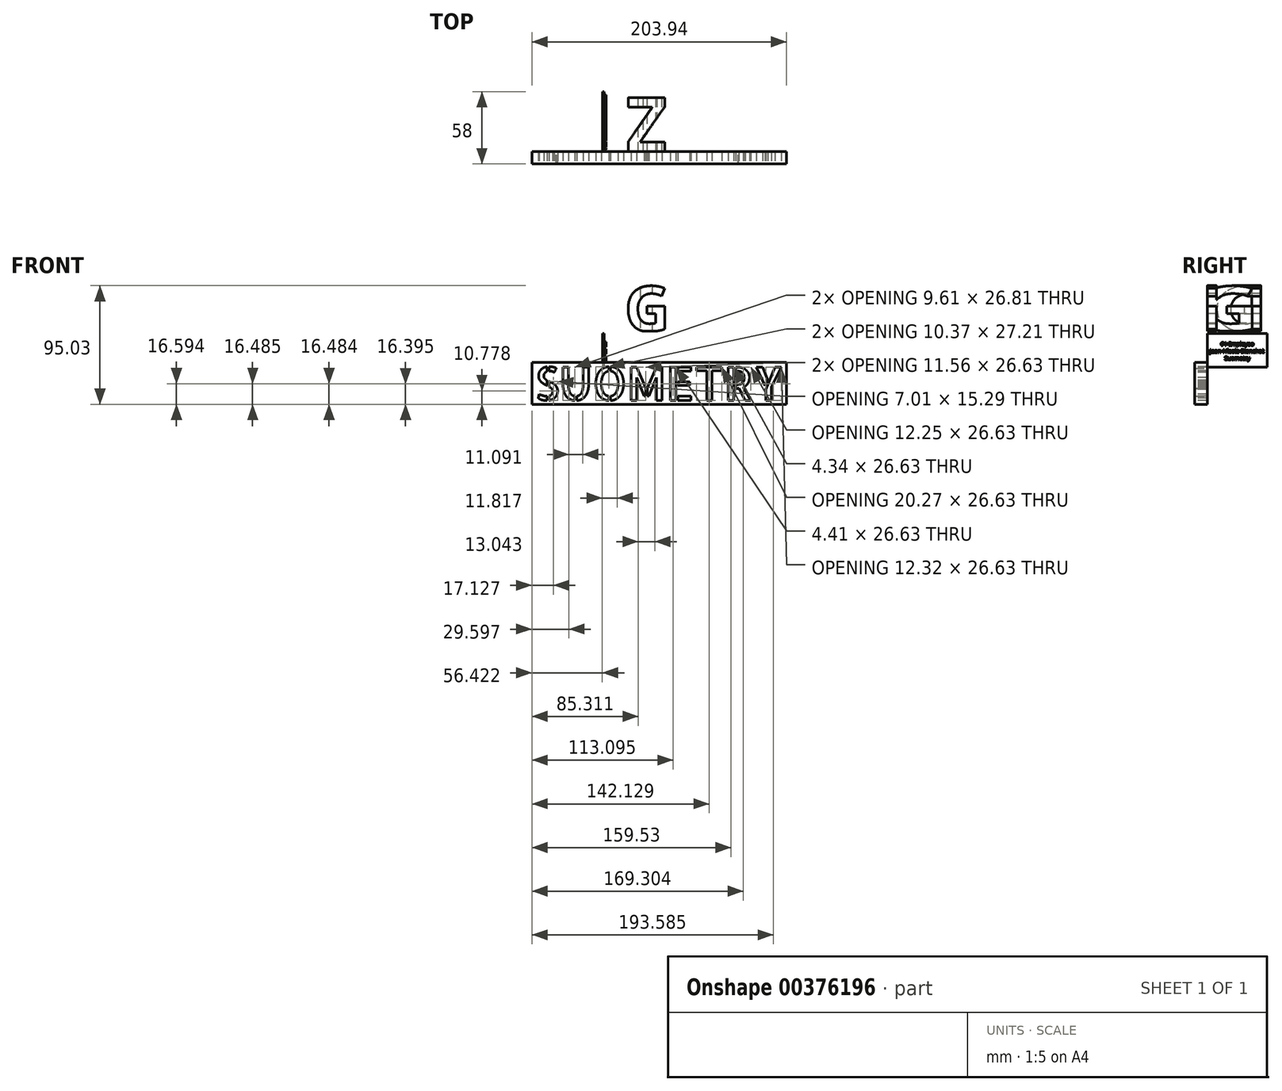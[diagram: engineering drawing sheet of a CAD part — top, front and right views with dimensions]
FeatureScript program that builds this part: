
annotation { "Feature Type Name" : "Feature", "Feature Type Description" : "" }
export const myFeature = defineFeature(function(context is Context, id is Id, definition is map)
    precondition{}
    {
        {
            var Q0;
            Q0=qCreatedBy(makeId("Front.planeOp"),FACE);
            var sketch = newSketch(context, id + "F0", { "sketchPlane" : qUnion([Q0])});
            skText(sketch, "E0", { "text": "V", "fontName": "Arimo-Bold.ttf"});
            const initialGuessF0  = {"E0": [-0.04078, 0, 1, 0, 0.04025]};
            skSetInitialGuess(sketch, initialGuessF0);
            skSolve(sketch);
        }
        {
            var Q0;
            Q0=qCreatedBy(makeId("Right.planeOp"),FACE);
            var sketch = newSketch(context, id + "F1", { "sketchPlane" : qUnion([Q0])});
            skText(sketch, "E1", { "text": "R", "fontName": "Arimo-Bold.ttf"});
            const initialGuessF1  = {"E1": [0, 0, 1, 0, 0.04]};
            skSetInitialGuess(sketch, initialGuessF1);
            skSolve(sketch);
        }
        {
            var Q0;
            Q0=makeQuery(id+"F0.imprint","IMPRINT",FACE,{"disambiguationData":[TD([[makeQuery(id+"F0.imprint","IMPRINT",EDGE,{"derivedFrom":sQuery(id+"F0.wireOp",EDGE,"E0.sketch_text.stroke-0")}),-1.0]])]});
            extrude(context, id + "F2", {"entities" : qUnion([Q0]), "oppositeDirection" : true, "depth" : 40.4 * mm});
        }
        {
            var Q0;
            Q0 = qSketchRegion(id + "F1", true);
            extrude(context, id + "F3", {"entities" : qUnion([Q0]), "operationType" : NewBodyOperationType.INTERSECT, "oppositeDirection" : true, "depth" : 45.3 * mm});
        }
        {
            var Q0;
            Q0=qCreatedBy(makeId("Front.planeOp"),FACE);
            var sketch = newSketch(context, id + "F4", { "sketchPlane" : qUnion([Q0])});
            skText(sketch, "E2", { "text": "G", "fontName": "OpenSans-Bold.ttf"});
            const initialGuessF4  = {"E2": [0.01758, 0, 1, 0, 0.03613]};
            skSetInitialGuess(sketch, initialGuessF4);
            skSolve(sketch);
        }
        {
            var Q0;
            Q0=qCreatedBy(makeId("Top.planeOp"),FACE);
            var sketch = newSketch(context, id + "F5", { "sketchPlane" : qUnion([Q0])});
            skText(sketch, "E3", { "text": "Z", "fontName": "OpenSans-Bold.ttf"});
            const initialGuessF5  = {"E3": [0.01774, 0, 1, 0, 0.04336]};
            skSetInitialGuess(sketch, initialGuessF5);
            skSolve(sketch);
        }
        {
            var Q0;
            Q0 = qSketchRegion(id + "F5", true);
            extrude(context, id + "F6", {"entities" : qUnion([Q0]), "depth" : 50 * mm});
        }
        {
            var Q0;
            Q0 = qSketchRegion(id + "F4", true);
            extrude(context, id + "F7", {"entities" : qUnion([Q0]), "operationType" : NewBodyOperationType.INTERSECT, "oppositeDirection" : true, "depth" : 60.3 * mm});
        }
        {
            var Q0;
            Q0=qCreatedBy(makeId("Front.planeOp"),FACE);
            var sketch = newSketch(context, id + "F8", { "sketchPlane" : qUnion([Q0])});
            skLineSegment(sketch, "E4.bottom", {"start": v(-56.6, -58.7) * mm, "end": v(147.34, -58.7) * mm});
            skLineSegment(sketch, "E4.top", {"start": v(-56.6, -25) * mm, "end": v(147.34, -25) * mm});
            skLineSegment(sketch, "E4.left", {"start": v(-56.6, -58.7) * mm, "end": v(-56.6, -25) * mm});
            skLineSegment(sketch, "E4.right", {"start": v(147.34, -58.7) * mm, "end": v(147.34, -25) * mm});
            skSolve(sketch);
        }
        {
            var Q0;
            Q0 = qSketchRegion(id + "F8", true);
            extrude(context, id + "F9", {"entities" : qUnion([Q0]), "depth" : 10 * mm});
        }
        {
            var Q0;
            Q0=makeQuery(id+"F9.opExtrude","CAP_FACE",FACE,{"disambiguationData":[OSD([sQuery(id+"F8.wireOp",EDGE,"E4.bottom"),sQuery(id+"F8.wireOp",EDGE,"E4.top"),sQuery(id+"F8.wireOp",EDGE,"E4.left"),sQuery(id+"F8.wireOp",EDGE,"E4.right")])],"isStart":false});
            var sketch = newSketch(context, id + "F10", { "sketchPlane" : qUnion([Q0])});
            skText(sketch, "E5", { "text": "SUOMETRY", "fontName": "AllertaStencil-Regular.ttf"});
            const initialGuessF10  = {"E5": [-0.05436, -0.05553, 1, 0, 0.02664]};
            skSetInitialGuess(sketch, initialGuessF10);
            skSolve(sketch);
        }
        {
            var Q0;
            Q0 = qSketchRegion(id + "F10", true);
            extrude(context, id + "F11", {"entities" : qUnion([Q0]), "operationType" : NewBodyOperationType.REMOVE, "oppositeDirection" : true, "depth" : 25 * mm});
        }
        {
            var Q0;
            Q0=qCreatedBy(makeId("Right.planeOp"),FACE);
            var sketch = newSketch(context, id + "F12", { "sketchPlane" : qUnion([Q0])});
            skLineSegment(sketch, "E6.bottom", {"start": v(0, -2.08) * mm, "end": v(48, -2.08) * mm});
            skLineSegment(sketch, "E6.top", {"start": v(0, -29.08) * mm, "end": v(48, -29.08) * mm});
            skLineSegment(sketch, "E6.left", {"start": v(0, -2.08) * mm, "end": v(0, -29.08) * mm});
            skLineSegment(sketch, "E6.right", {"start": v(48, -2.08) * mm, "end": v(48, -29.08) * mm});
            skSolve(sketch);
        }
        {
            var Q0;
            Q0=makeQuery(id+"F12.imprint","IMPRINT",FACE,{"disambiguationData":[TD([[makeQuery(id+"F12.imprint","IMPRINT",EDGE,{"derivedFrom":sQuery(id+"F12.wireOp",EDGE,"E6.bottom")}),-1.0]])]});
            extrude(context, id + "F13", {"entities" : qUnion([Q0]), "depth" : 1.2 * mm});
        }
        {
            var Q0;
            Q0=makeQuery(id+"F13.opExtrude","CAP_FACE",FACE,{"disambiguationData":[OSD([sQuery(id+"F12.wireOp",EDGE,"E6.bottom"),sQuery(id+"F12.wireOp",EDGE,"E6.top"),sQuery(id+"F12.wireOp",EDGE,"E6.left"),sQuery(id+"F12.wireOp",EDGE,"E6.right")])],"isStart":false});
            var sketch = newSketch(context, id + "F14", { "sketchPlane" : qUnion([Q0])});
            skSolve(sketch);
        }
        {
            var Q0;
            {var subQ3=sQuery(id+"F12.wireOp",EDGE,"E6.bottom");Q0=makeQuery(id+"F14.imprint","IMPRINT",FACE,{"disambiguationData":[TD([[makeQuery(id+"F14.imprint","IMPRINT",EDGE,{"derivedFrom":makeQuery(id+"F13.opExtrude","CAP_EDGE",EDGE,{"disambiguationData":[OSD([subQ3])],"isStart":false})}),-1.0]])]});}
            var sketch = newSketch(context, id + "F15", { "sketchPlane" : qUnion([Q0])});
            skText(sketch, "E7", { "text": "        #1 Employee\nJean-Nicola Blanchet\n           Suometry", "fontName": "OpenSans-Bold.ttf"});
            const initialGuessF15  = {"E7": [0.00189, -0.0118, 1, 0, 0.00303]};
            skSetInitialGuess(sketch, initialGuessF15);
            skSolve(sketch);
        }
        {
            var Q0;
            Q0 = qSketchRegion(id + "F15", true);
            extrude(context, id + "F16", {"entities" : qUnion([Q0]), "operationType" : NewBodyOperationType.ADD, "depth" : 1.6 * mm});
        }
    });
